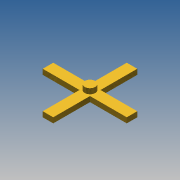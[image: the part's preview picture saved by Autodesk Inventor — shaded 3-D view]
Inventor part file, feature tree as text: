
AUTODESK INVENTOR PART (.ipt)
format: ipt  version: 2014 SP1 (Build 180222100, 222)  size: 95,232 bytes
history: native  units: in
note: dims shown in document units (in); Inventor stores cm internally (conversion verified against a paired STEP export)
features: extrude x2, sketch x2
ambient origin geometry x8: Origin, YZ Plane, XZ Plane, XY Plane, X Axis, Y Axis, Z Axis, Center Point
bodies: Solid1 (feature_tree)
feature tree (4):
  extrude  "Extrusion1"  Depth=1.0in
  extrude  "Extrusion2"  Depth=8.0in
  sketch  "Sketch1"  dims[d0=8.0in d1=1.0in]
  sketch  "Sketch2"  dims[d2=1.0in d3=8.0in d4=0.5in d5=0.0in d7=1.0in d8=0.5in d9=0.0in]
